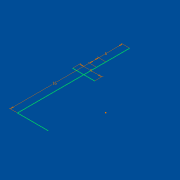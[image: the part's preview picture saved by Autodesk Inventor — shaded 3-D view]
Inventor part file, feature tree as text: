
AUTODESK INVENTOR PART (.ipt)
format: ipt  version: 2016 (Build 200138000, 138)  size: 59,904 bytes
history: native  units: mm
features: sketch x1
ambient origin geometry x8: Origin, YZ Plane, XZ Plane, XY Plane, X Axis, Y Axis, Z Axis, Center Point
feature tree (1):
  sketch  "Sketch1"  dims[d0=16.0mm d1=6.0mm d2=4.0mm]
